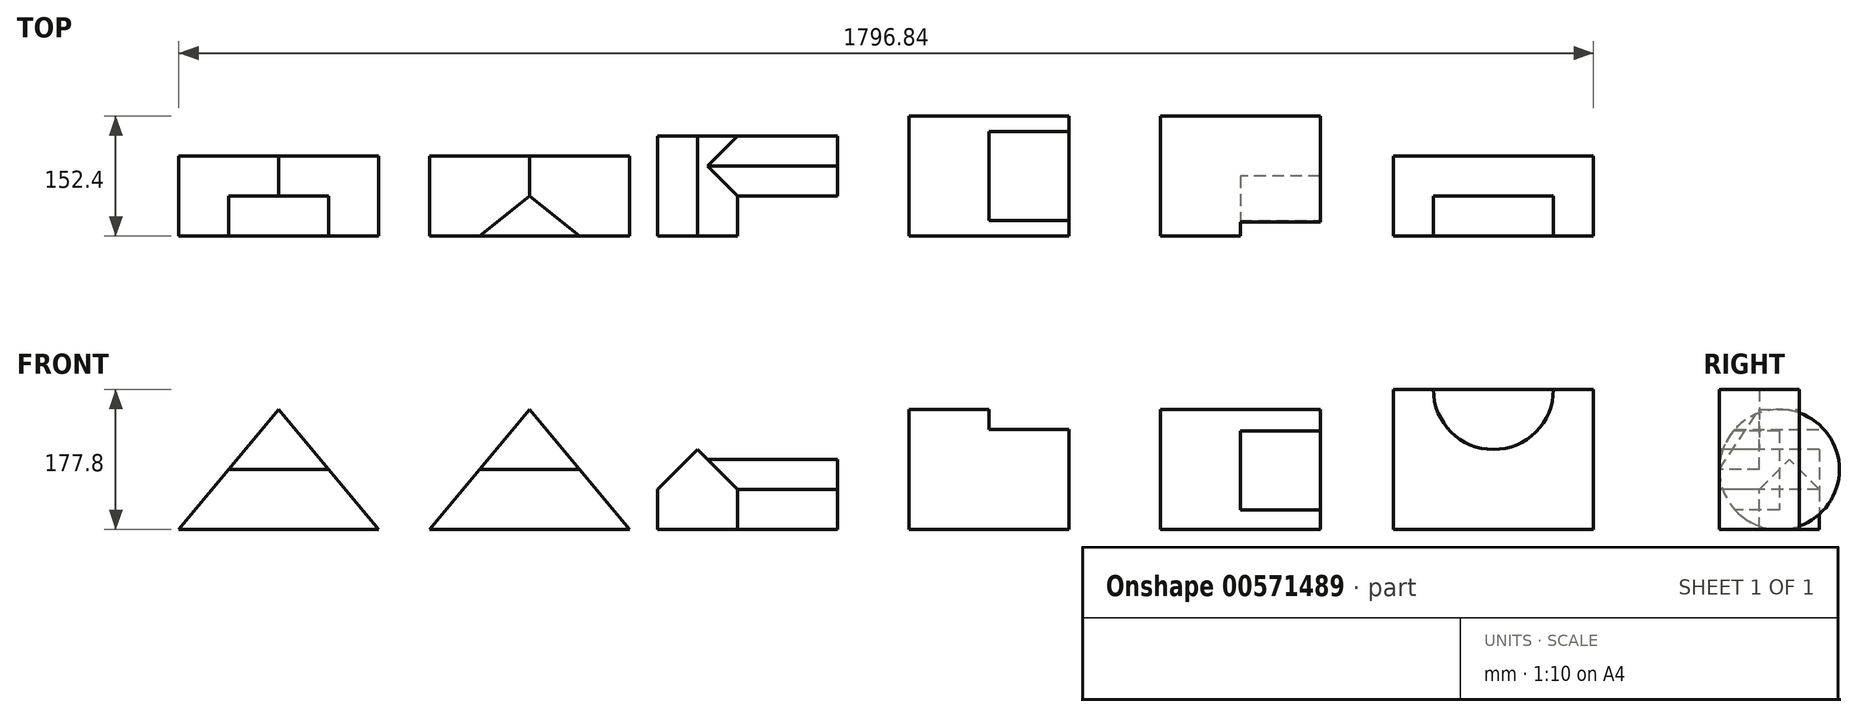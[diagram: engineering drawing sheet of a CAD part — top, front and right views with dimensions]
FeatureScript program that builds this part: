
annotation { "Feature Type Name" : "Feature", "Feature Type Description" : "" }
export const myFeature = defineFeature(function(context is Context, id is Id, definition is map)
    precondition{}
    {
        {
            var Q0;
            Q0=qCreatedBy(makeId("Front.planeOp"),FACE);
            var sketch = newSketch(context, id + "F0", { "sketchPlane" : qUnion([Q0])});
            skLineSegment(sketch, "E0", {"start": v(103.19, 0) * mm, "end": v(103.19, 152.4) * mm});
            skLineSegment(sketch, "E1", {"start": v(103.19, 152.4) * mm, "end": v(357.19, 152.4) * mm});
            skLineSegment(sketch, "E2", {"start": v(357.19, 152.4) * mm, "end": v(357.19, 0) * mm});
            skLineSegment(sketch, "E3", {"start": v(357.19, 0) * mm, "end": v(103.19, 0) * mm});
            skSolve(sketch);
        }
        {
            var Q0;
            Q0=makeQuery(id+"F0.imprint","IMPRINT",FACE,{"disambiguationData":[TD([[makeQuery(id+"F0.imprint","IMPRINT",EDGE,{"derivedFrom":sQuery(id+"F0.wireOp",EDGE,"E0")}),-1.0]])]});
            extrude(context, id + "F1", {"entities" : qUnion([Q0]), "oppositeDirection" : true, "depth" : 101.6 * mm, "offsetDistance" : 25.4 * mm});
        }
        {
            var Q0;
            Q0=makeQuery(id+"F1.opExtrude","CAP_FACE",FACE,{"disambiguationData":[OSD([sQuery(id+"F0.wireOp",EDGE,"E0"),sQuery(id+"F0.wireOp",EDGE,"E1"),sQuery(id+"F0.wireOp",EDGE,"E2"),sQuery(id+"F0.wireOp",EDGE,"E3")])],"isStart":true});
            var sketch = newSketch(context, id + "F2", { "sketchPlane" : qUnion([Q0])});
            skLineSegment(sketch, "E4", {"start": v(103.19, 0) * mm, "end": v(230.19, 152.4) * mm});
            skLineSegment(sketch, "E5", {"start": v(230.19, 152.4) * mm, "end": v(357.19, 0) * mm});
            skLineSegment(sketch, "E6", {"start": v(166.69, 76.2) * mm, "end": v(293.69, 76.2) * mm});
            skSolve(sketch);
        }
        {
            var Q0;
            {var subQ1=makeQuery(id+"F1.opExtrude","CAP_EDGE",EDGE,{"disambiguationData":[OSD([sQuery(id+"F0.wireOp",EDGE,"E0")])],"isStart":true});Q0=makeQuery(id+"F2.imprint","IMPRINT",FACE,{"disambiguationData":[TD([[makeQuery(id+"F2.imprint","IMPRINT",EDGE,{"derivedFrom":subQ1}),-1.0]])]});}
            extrude(context, id + "F3", {"entities" : qUnion([Q0]), "operationType" : NewBodyOperationType.REMOVE, "oppositeDirection" : true, "depth" : 171.45 * mm, "offsetDistance" : 25.4 * mm});
        }
        {
            var Q0;
            Q0=makeQuery(id+"F1.opExtrude","CAP_FACE",FACE,{"disambiguationData":[OSD([sQuery(id+"F0.wireOp",EDGE,"E0"),sQuery(id+"F0.wireOp",EDGE,"E1"),sQuery(id+"F0.wireOp",EDGE,"E2"),sQuery(id+"F0.wireOp",EDGE,"E3")])],"isStart":true});
            var sketch = newSketch(context, id + "F4", { "sketchPlane" : qUnion([Q0])});
            skLineSegment(sketch, "E7", {"start": v(357.19, 0) * mm, "end": v(230.19, 152.4) * mm});
            skLineSegment(sketch, "E8", {"start": v(293.69, 76.2) * mm, "end": v(166.69, 76.2) * mm});
            skSolve(sketch);
        }
        {
            var Q0;
            {var subQ3=sQuery(id+"F4.wireOp",EDGE,"E8");Q0=makeQuery(id+"F4.imprint","IMPRINT",FACE,{"disambiguationData":[TD([[makeQuery(id+"F4.imprint","IMPRINT",EDGE,{"derivedFrom":subQ3}),-1.0]])]});}
            extrude(context, id + "F5", {"entities" : qUnion([Q0]), "operationType" : NewBodyOperationType.REMOVE, "oppositeDirection" : true, "depth" : 50.8 * mm, "offsetDistance" : 25.4 * mm});
        }
        {
            var Q0;
            Q0=makeQuery(id+"F1.opExtrude","CAP_FACE",FACE,{"disambiguationData":[OSD([sQuery(id+"F0.wireOp",EDGE,"E0"),sQuery(id+"F0.wireOp",EDGE,"E1"),sQuery(id+"F0.wireOp",EDGE,"E2"),sQuery(id+"F0.wireOp",EDGE,"E3")])],"isStart":true});
            var sketch = newSketch(context, id + "F6", { "sketchPlane" : qUnion([Q0])});
            skLineSegment(sketch, "E9", {"start": v(293.69, 76.2) * mm, "end": v(357.19, 0) * mm});
            skSolve(sketch);
        }
        {
            var Q0;
            Q0=makeQuery(id+"F6.imprint","IMPRINT",FACE,{"disambiguationData":[TD([[makeQuery(id+"F6.imprint","IMPRINT",EDGE,{"derivedFrom":sQuery(id+"F6.wireOp",EDGE,"E9")}),1.0]])]});
            extrude(context, id + "F7", {"entities" : qUnion([Q0]), "operationType" : NewBodyOperationType.REMOVE, "oppositeDirection" : true, "depth" : 181.1 * mm, "offsetDistance" : 25.4 * mm});
        }
        {
            var Q0;
            Q0=qCreatedBy(makeId("Front.planeOp"),FACE);
            var sketch = newSketch(context, id + "F8", { "sketchPlane" : qUnion([Q0])});
            skLineSegment(sketch, "E10", {"start": v(421.92, 0) * mm, "end": v(421.92, 152.4) * mm});
            skLineSegment(sketch, "E11", {"start": v(421.92, 152.4) * mm, "end": v(675.92, 152.4) * mm});
            skLineSegment(sketch, "E12", {"start": v(675.92, 152.4) * mm, "end": v(675.92, 0) * mm});
            skLineSegment(sketch, "E13", {"start": v(675.92, 0) * mm, "end": v(421.92, 0) * mm});
            skSolve(sketch);
        }
        {
            var Q0;
            Q0=makeQuery(id+"F8.imprint","IMPRINT",FACE,{"disambiguationData":[TD([[makeQuery(id+"F8.imprint","IMPRINT",EDGE,{"derivedFrom":sQuery(id+"F8.wireOp",EDGE,"E10")}),-1.0]])]});
            extrude(context, id + "F9", {"entities" : qUnion([Q0]), "oppositeDirection" : true, "depth" : 101.6 * mm, "offsetDistance" : 25.4 * mm});
        }
        {
            var Q0;
            Q0=makeQuery(id+"F9.opExtrude","SWEPT_FACE",FACE,{"disambiguationData":[OSD([sQuery(id+"F8.wireOp",EDGE,"E12")])]});
            var sketch = newSketch(context, id + "F10", { "sketchPlane" : qUnion([Q0])});
            skLineSegment(sketch, "E14", {"start": v(0, 76.2) * mm, "end": v(50.8, 152.4) * mm});
            skSolve(sketch);
        }
        {
            var Q0;
            {var subQ0=sQuery(id+"F10.wireOp",EDGE,"E14");Q0=makeQuery(id+"F10.imprint","IMPRINT",FACE,{"disambiguationData":[TD([[makeQuery(id+"F10.imprint","IMPRINT",EDGE,{"derivedFrom":subQ0}),1.0]])]});}
            extrude(context, id + "F11", {"entities" : qUnion([Q0]), "operationType" : NewBodyOperationType.REMOVE, "oppositeDirection" : true, "depth" : 317.75 * mm, "offsetDistance" : 25.4 * mm});
        }
        {
            var Q0;
            Q0=makeQuery(id+"F9.opExtrude","CAP_FACE",FACE,{"disambiguationData":[OSD([sQuery(id+"F8.wireOp",EDGE,"E10"),sQuery(id+"F8.wireOp",EDGE,"E11"),sQuery(id+"F8.wireOp",EDGE,"E12"),sQuery(id+"F8.wireOp",EDGE,"E13")])],"isStart":false});
            var sketch = newSketch(context, id + "F12", { "sketchPlane" : qUnion([Q0])});
            skLineSegment(sketch, "E15", {"start": v(-675.92, 0) * mm, "end": v(-548.92, 152.4) * mm});
            skSolve(sketch);
        }
        {
            var Q0;
            {var subQ0=sQuery(id+"F12.wireOp",EDGE,"E15");Q0=makeQuery(id+"F12.imprint","IMPRINT",FACE,{"disambiguationData":[TD([[makeQuery(id+"F12.imprint","IMPRINT",EDGE,{"derivedFrom":subQ0}),1.0]])]});}
            extrude(context, id + "F13", {"entities" : qUnion([Q0]), "operationType" : NewBodyOperationType.REMOVE, "oppositeDirection" : true, "depth" : 144.78 * mm, "offsetDistance" : 25.4 * mm});
        }
        {
            var Q0;
            Q0=makeQuery(id+"F9.opExtrude","CAP_FACE",FACE,{"disambiguationData":[OSD([sQuery(id+"F8.wireOp",EDGE,"E10"),sQuery(id+"F8.wireOp",EDGE,"E11"),sQuery(id+"F8.wireOp",EDGE,"E12"),sQuery(id+"F8.wireOp",EDGE,"E13")])],"isStart":false});
            var sketch = newSketch(context, id + "F14", { "sketchPlane" : qUnion([Q0])});
            skLineSegment(sketch, "E16", {"start": v(-548.92, 152.4) * mm, "end": v(-421.92, 0) * mm});
            skSolve(sketch);
        }
        {
            var Q0;
            Q0=makeQuery(id+"F14.imprint","IMPRINT",FACE,{"disambiguationData":[TD([[makeQuery(id+"F14.imprint","IMPRINT",EDGE,{"derivedFrom":sQuery(id+"F14.wireOp",EDGE,"E16")}),1.0]])]});
            extrude(context, id + "F15", {"entities" : qUnion([Q0]), "operationType" : NewBodyOperationType.REMOVE, "oppositeDirection" : true, "depth" : 111.76 * mm, "offsetDistance" : 25.4 * mm});
        }
        {
            var Q0;
            Q0=qCreatedBy(makeId("Top.planeOp"),FACE);
            var sketch = newSketch(context, id + "F16", { "sketchPlane" : qUnion([Q0])});
            skLineSegment(sketch, "E17", {"start": v(711.33, 0) * mm, "end": v(711.33, 127) * mm});
            skLineSegment(sketch, "E18", {"start": v(711.33, 127) * mm, "end": v(939.93, 127) * mm});
            skLineSegment(sketch, "E19", {"start": v(939.93, 127) * mm, "end": v(939.93, 0) * mm});
            skLineSegment(sketch, "E20", {"start": v(939.93, 0) * mm, "end": v(711.33, 0) * mm});
            skSolve(sketch);
        }
        {
            var Q0;
            Q0=makeQuery(id+"F16.imprint","IMPRINT",FACE,{"disambiguationData":[TD([[makeQuery(id+"F16.imprint","IMPRINT",EDGE,{"derivedFrom":sQuery(id+"F16.wireOp",EDGE,"E17")}),-1.0]])]});
            extrude(context, id + "F17", {"entities" : qUnion([Q0]), "depth" : 101.6 * mm, "offsetDistance" : 25.4 * mm});
        }
        {
            var Q0;
            Q0=makeQuery(id+"F17.opExtrude","CAP_FACE",FACE,{"disambiguationData":[OSD([sQuery(id+"F16.wireOp",EDGE,"E17"),sQuery(id+"F16.wireOp",EDGE,"E18"),sQuery(id+"F16.wireOp",EDGE,"E19"),sQuery(id+"F16.wireOp",EDGE,"E20")])],"isStart":false});
            var sketch = newSketch(context, id + "F18", { "sketchPlane" : qUnion([Q0])});
            skLineSegment(sketch, "E21.bottom", {"start": v(939.93, 0) * mm, "end": v(812.93, 0) * mm});
            skLineSegment(sketch, "E21.top", {"start": v(939.93, 50.8) * mm, "end": v(812.93, 50.8) * mm});
            skLineSegment(sketch, "E21.left", {"start": v(939.93, 0) * mm, "end": v(939.93, 50.8) * mm});
            skLineSegment(sketch, "E21.right", {"start": v(812.93, 0) * mm, "end": v(812.93, 50.8) * mm});
            skSolve(sketch);
        }
        {
            var Q0;
            Q0=makeQuery(id+"F18.imprint","IMPRINT",FACE,{"disambiguationData":[TD([[makeQuery(id+"F18.imprint","IMPRINT",EDGE,{"derivedFrom":sQuery(id+"F18.wireOp",EDGE,"E21.bottom")}),-1.0]])]});
            extrude(context, id + "F19", {"entities" : qUnion([Q0]), "operationType" : NewBodyOperationType.REMOVE, "oppositeDirection" : true, "depth" : 124.46 * mm, "offsetDistance" : 25.4 * mm});
        }
        {
            var Q0;
            Q0=makeQuery(id+"F17.opExtrude","SWEPT_FACE",FACE,{"disambiguationData":[OSD([sQuery(id+"F16.wireOp",EDGE,"E19")])]});
            var sketch = newSketch(context, id + "F20", { "sketchPlane" : qUnion([Q0])});
            skLineSegment(sketch, "E22.bottom", {"start": v(50.8, 101.6) * mm, "end": v(127, 101.6) * mm});
            skLineSegment(sketch, "E22.top", {"start": v(50.8, 88.9) * mm, "end": v(127, 88.9) * mm});
            skLineSegment(sketch, "E22.left", {"start": v(50.8, 101.6) * mm, "end": v(50.8, 88.9) * mm});
            skLineSegment(sketch, "E22.right", {"start": v(127, 101.6) * mm, "end": v(127, 88.9) * mm});
            skSolve(sketch);
        }
        {
            var Q0;
            Q0=makeQuery(id+"F20.imprint","IMPRINT",FACE,{"disambiguationData":[TD([[makeQuery(id+"F20.imprint","IMPRINT",EDGE,{"derivedFrom":sQuery(id+"F20.wireOp",EDGE,"E22.bottom")}),1.0]])]});
            extrude(context, id + "F21", {"entities" : qUnion([Q0]), "operationType" : NewBodyOperationType.REMOVE, "oppositeDirection" : true, "depth" : 127 * mm, "offsetDistance" : 25.4 * mm});
        }
        {
            var Q0;
            Q0=makeQuery(id+"F17.opExtrude","SWEPT_FACE",FACE,{"disambiguationData":[OSD([sQuery(id+"F16.wireOp",EDGE,"E20")])]});
            var sketch = newSketch(context, id + "F22", { "sketchPlane" : qUnion([Q0])});
            skLineSegment(sketch, "E23", {"start": v(762.13, 101.6) * mm, "end": v(711.33, 50.8) * mm});
            skSolve(sketch);
        }
        {
            var Q0;
            {var subQ0=sQuery(id+"F22.wireOp",EDGE,"E23");Q0=makeQuery(id+"F22.imprint","IMPRINT",FACE,{"disambiguationData":[TD([[makeQuery(id+"F22.imprint","IMPRINT",EDGE,{"derivedFrom":subQ0}),-1.0]])]});}
            extrude(context, id + "F23", {"entities" : qUnion([Q0]), "operationType" : NewBodyOperationType.REMOVE, "oppositeDirection" : true, "depth" : 210.82 * mm, "offsetDistance" : 25.4 * mm});
        }
        {
            var Q0;
            Q0=makeQuery(id+"F17.opExtrude","SWEPT_FACE",FACE,{"disambiguationData":[OSD([sQuery(id+"F16.wireOp",EDGE,"E19")])]});
            var sketch = newSketch(context, id + "F24", { "sketchPlane" : qUnion([Q0])});
            skLineSegment(sketch, "E24", {"start": v(127, 0) * mm, "end": v(127, 50.8) * mm});
            skLineSegment(sketch, "E25", {"start": v(127, 50.8) * mm, "end": v(88.9, 88.9) * mm});
            skSolve(sketch);
        }
        {
            var Q0;
            {var subQ0=sQuery(id+"F24.wireOp",EDGE,"E25");Q0=makeQuery(id+"F24.imprint","IMPRINT",FACE,{"disambiguationData":[TD([[makeQuery(id+"F24.imprint","IMPRINT",EDGE,{"derivedFrom":subQ0}),-1.0]])]});}
            extrude(context, id + "F25", {"entities" : qUnion([Q0]), "operationType" : NewBodyOperationType.REMOVE, "oppositeDirection" : true, "depth" : 127 * mm, "offsetDistance" : 25.4 * mm});
        }
        {
            var Q0;
            Q0=makeQuery(id+"F17.opExtrude","SWEPT_FACE",FACE,{"disambiguationData":[OSD([sQuery(id+"F16.wireOp",EDGE,"E19")])]});
            var sketch = newSketch(context, id + "F26", { "sketchPlane" : qUnion([Q0])});
            skLineSegment(sketch, "E26", {"start": v(50.8, 0) * mm, "end": v(50.8, 50.8) * mm});
            skLineSegment(sketch, "E27", {"start": v(50.8, 50.8) * mm, "end": v(88.9, 88.9) * mm});
            skSolve(sketch);
        }
        {
            var Q0;
            {var subQ0=sQuery(id+"F26.wireOp",EDGE,"E27");Q0=makeQuery(id+"F26.imprint","IMPRINT",FACE,{"disambiguationData":[TD([[makeQuery(id+"F26.imprint","IMPRINT",EDGE,{"derivedFrom":subQ0}),1.0]])]});}
            extrude(context, id + "F27", {"entities" : qUnion([Q0]), "operationType" : NewBodyOperationType.REMOVE, "oppositeDirection" : true, "depth" : 127 * mm, "offsetDistance" : 25.4 * mm});
        }
        {
            var Q0;
            Q0=makeQuery(id+"F17.opExtrude","SWEPT_FACE",FACE,{"disambiguationData":[OSD([sQuery(id+"F16.wireOp",EDGE,"E20")])]});
            var sketch = newSketch(context, id + "F28", { "sketchPlane" : qUnion([Q0])});
            skLineSegment(sketch, "E28", {"start": v(812.93, 50.8) * mm, "end": v(762.13, 101.6) * mm});
            skSolve(sketch);
        }
        {
            var Q0;
            {var subQ0=sQuery(id+"F28.wireOp",EDGE,"E28");Q0=makeQuery(id+"F28.imprint","IMPRINT",FACE,{"disambiguationData":[TD([[makeQuery(id+"F28.imprint","IMPRINT",EDGE,{"derivedFrom":subQ0}),-1.0]])]});}
            extrude(context, id + "F29", {"entities" : qUnion([Q0]), "operationType" : NewBodyOperationType.REMOVE, "oppositeDirection" : true, "depth" : 157.48 * mm, "offsetDistance" : 25.4 * mm});
        }
        {
            var Q0;
            Q0=makeQuery(id+"F17.opExtrude","SWEPT_FACE",FACE,{"disambiguationData":[OSD([sQuery(id+"F16.wireOp",EDGE,"E19")])]});
            var sketch = newSketch(context, id + "F30", { "sketchPlane" : qUnion([Q0])});
            skLineSegment(sketch, "E29", {"start": v(50.8, 50.8) * mm, "end": v(127, 50.8) * mm});
            skSolve(sketch);
        }
        {
            var Q0;
            Q0=makeQuery(id+"F30.imprint","IMPRINT",FACE,{"disambiguationData":[TD([[makeQuery(id+"F30.imprint","IMPRINT",EDGE,{"derivedFrom":sQuery(id+"F30.wireOp",EDGE,"E29")}),1.0]])]});
            extrude(context, id + "F31", {"entities" : qUnion([Q0]), "operationType" : NewBodyOperationType.ADD, "oppositeDirection" : true, "depth" : 177.8 * mm, "offsetDistance" : 25.4 * mm});
        }
        {
            var Q0;
            Q0=qCreatedBy(makeId("Top.planeOp"),FACE);
            var sketch = newSketch(context, id + "F32", { "sketchPlane" : qUnion([Q0])});
            skLineSegment(sketch, "E30", {"start": v(1030.46, 0) * mm, "end": v(1030.46, 152.4) * mm});
            skLineSegment(sketch, "E31", {"start": v(1030.46, 152.4) * mm, "end": v(1233.66, 152.4) * mm});
            skLineSegment(sketch, "E32", {"start": v(1233.66, 152.4) * mm, "end": v(1233.66, 0) * mm});
            skLineSegment(sketch, "E33", {"start": v(1233.66, 0) * mm, "end": v(1030.46, 0) * mm});
            skSolve(sketch);
        }
        {
            var Q0;
            Q0=makeQuery(id+"F32.imprint","IMPRINT",FACE,{"disambiguationData":[TD([[makeQuery(id+"F32.imprint","IMPRINT",EDGE,{"derivedFrom":sQuery(id+"F32.wireOp",EDGE,"E30")}),-1.0]])]});
            extrude(context, id + "F33", {"entities" : qUnion([Q0]), "depth" : 152.4 * mm, "offsetDistance" : 25.4 * mm});
        }
        {
            var Q0;
            Q0=makeQuery(id+"F33.opExtrude","SWEPT_FACE",FACE,{"disambiguationData":[OSD([sQuery(id+"F32.wireOp",EDGE,"E32")])]});
            var sketch = newSketch(context, id + "F34", { "sketchPlane" : qUnion([Q0])});
            skLineSegment(sketch, "E34.bottom", {"start": v(0, 152.4) * mm, "end": v(152.4, 152.4) * mm});
            skLineSegment(sketch, "E34.top", {"start": v(0, 127) * mm, "end": v(152.4, 127) * mm});
            skLineSegment(sketch, "E34.left", {"start": v(0, 152.4) * mm, "end": v(0, 127) * mm});
            skLineSegment(sketch, "E34.right", {"start": v(152.4, 152.4) * mm, "end": v(152.4, 127) * mm});
            skSolve(sketch);
        }
        {
            var Q0;
            Q0=makeQuery(id+"F34.imprint","IMPRINT",FACE,{"disambiguationData":[TD([[makeQuery(id+"F34.imprint","IMPRINT",EDGE,{"derivedFrom":sQuery(id+"F34.wireOp",EDGE,"E34.bottom")}),1.0]])]});
            extrude(context, id + "F35", {"entities" : qUnion([Q0]), "operationType" : NewBodyOperationType.REMOVE, "oppositeDirection" : true, "depth" : 101.6 * mm, "offsetDistance" : 25.4 * mm});
        }
        {
            var Q0;
            Q0=makeQuery(id+"F33.opExtrude","CAP_EDGE",EDGE,{"disambiguationData":[OSD([sQuery(id+"F32.wireOp",EDGE,"E31")])],"isStart":false});
            fillet(context, id + "F36", {"entities" : qUnion([Q0]), "radius" : 76.2 * mm, "tangentPropagation" : true, "allowEdgeOverflow" : false});
        }
        {
            var Q0;
            Q0=makeQuery(id+"F33.opExtrude","CAP_EDGE",EDGE,{"disambiguationData":[OSD([sQuery(id+"F32.wireOp",EDGE,"E33")])],"isStart":false});
            fillet(context, id + "F37", {"entities" : qUnion([Q0]), "radius" : 76.2 * mm, "tangentPropagation" : true, "allowEdgeOverflow" : false});
        }
        {
            var Q0;
            Q0=makeQuery(id+"F33.opExtrude","CAP_EDGE",EDGE,{"disambiguationData":[OSD([sQuery(id+"F32.wireOp",EDGE,"E31")])],"isStart":true});
            fillet(context, id + "F38", {"entities" : qUnion([Q0]), "radius" : 76.2 * mm, "tangentPropagation" : true, "allowEdgeOverflow" : false});
        }
        {
            var Q0;
            Q0=makeQuery(id+"F33.opExtrude","CAP_EDGE",EDGE,{"disambiguationData":[OSD([sQuery(id+"F32.wireOp",EDGE,"E33")])],"isStart":true});
            fillet(context, id + "F39", {"entities" : qUnion([Q0]), "radius" : 76.2 * mm, "tangentPropagation" : true, "allowEdgeOverflow" : false});
        }
        {
            var Q0;
            Q0=qCreatedBy(makeId("Top.planeOp"),FACE);
            var sketch = newSketch(context, id + "F40", { "sketchPlane" : qUnion([Q0])});
            skLineSegment(sketch, "E35", {"start": v(1349.86, 0) * mm, "end": v(1349.86, 152.4) * mm});
            skLineSegment(sketch, "E36", {"start": v(1349.86, 152.4) * mm, "end": v(1553.06, 152.4) * mm});
            skLineSegment(sketch, "E37", {"start": v(1553.06, 152.4) * mm, "end": v(1553.06, 0) * mm});
            skLineSegment(sketch, "E38", {"start": v(1553.06, 0) * mm, "end": v(1349.86, 0) * mm});
            skSolve(sketch);
        }
        {
            var Q0;
            Q0=makeQuery(id+"F40.imprint","IMPRINT",FACE,{"disambiguationData":[TD([[makeQuery(id+"F40.imprint","IMPRINT",EDGE,{"derivedFrom":sQuery(id+"F40.wireOp",EDGE,"E35")}),-1.0]])]});
            extrude(context, id + "F41", {"entities" : qUnion([Q0]), "depth" : 152.4 * mm, "offsetDistance" : 25.4 * mm});
        }
        {
            var Q0;
            Q0=makeQuery(id+"F41.opExtrude","SWEPT_FACE",FACE,{"disambiguationData":[OSD([sQuery(id+"F40.wireOp",EDGE,"E38")])]});
            var sketch = newSketch(context, id + "F42", { "sketchPlane" : qUnion([Q0])});
            skLineSegment(sketch, "E39", {"start": v(1553.06, 124.92) * mm, "end": v(1451.52, 124.92) * mm});
            skLineSegment(sketch, "E40", {"start": v(1451.52, 124.92) * mm, "end": v(1451.52, 25.04) * mm});
            skLineSegment(sketch, "E41", {"start": v(1451.52, 25.04) * mm, "end": v(1553.06, 25.04) * mm});
            skSolve(sketch);
        }
        {
            var Q0;
            {var subQ0=sQuery(id+"F42.wireOp",EDGE,"E39");Q0=makeQuery(id+"F42.imprint","IMPRINT",FACE,{"disambiguationData":[TD([[makeQuery(id+"F42.imprint","IMPRINT",EDGE,{"derivedFrom":subQ0}),1.0]])]});}
            extrude(context, id + "F43", {"entities" : qUnion([Q0]), "operationType" : NewBodyOperationType.REMOVE, "oppositeDirection" : true, "depth" : 76.2 * mm, "offsetDistance" : 25.4 * mm});
        }
        {
            var Q0;
            Q0=makeQuery(id+"F41.opExtrude","CAP_EDGE",EDGE,{"disambiguationData":[OSD([sQuery(id+"F40.wireOp",EDGE,"E38")])],"isStart":false});
            fillet(context, id + "F44", {"entities" : qUnion([Q0]), "radius" : 76.2 * mm, "tangentPropagation" : true, "allowEdgeOverflow" : false});
        }
        {
            var Q0;
            Q0=makeQuery(id+"F41.opExtrude","CAP_EDGE",EDGE,{"disambiguationData":[OSD([sQuery(id+"F40.wireOp",EDGE,"E38")])],"isStart":true});
            var Q1;
            Q1=makeQuery(id+"F41.opExtrude","CAP_EDGE",EDGE,{"disambiguationData":[OSD([sQuery(id+"F40.wireOp",EDGE,"E36")])],"isStart":false});
            var Q2;
            Q2=makeQuery(id+"F41.opExtrude","CAP_EDGE",EDGE,{"disambiguationData":[OSD([sQuery(id+"F40.wireOp",EDGE,"E36")])],"isStart":true});
            fillet(context, id + "F45", {"entities" : qUnion([Q0, Q1, Q2]), "radius" : 76.2 * mm, "tangentPropagation" : true, "allowEdgeOverflow" : false});
        }
        {
            var Q0;
            Q0=qCreatedBy(makeId("Top.planeOp"),FACE);
            var sketch = newSketch(context, id + "F46", { "sketchPlane" : qUnion([Q0])});
            skLineSegment(sketch, "E42", {"start": v(1646.03, 0) * mm, "end": v(1646.03, 101.6) * mm});
            skLineSegment(sketch, "E43", {"start": v(1646.03, 101.6) * mm, "end": v(1900.03, 101.6) * mm});
            skLineSegment(sketch, "E44", {"start": v(1900.03, 101.6) * mm, "end": v(1900.03, 0) * mm});
            skLineSegment(sketch, "E45", {"start": v(1900.03, 0) * mm, "end": v(1646.03, 0) * mm});
            skSolve(sketch);
        }
        {
            var Q0;
            Q0=makeQuery(id+"F46.imprint","IMPRINT",FACE,{"disambiguationData":[TD([[makeQuery(id+"F46.imprint","IMPRINT",EDGE,{"derivedFrom":sQuery(id+"F46.wireOp",EDGE,"E42")}),-1.0]])]});
            extrude(context, id + "F47", {"entities" : qUnion([Q0]), "depth" : 177.8 * mm, "offsetDistance" : 25.4 * mm});
        }
        {
            var Q0;
            Q0=makeQuery(id+"F47.opExtrude","SWEPT_FACE",FACE,{"disambiguationData":[OSD([sQuery(id+"F46.wireOp",EDGE,"E45")])]});
            var sketch = newSketch(context, id + "F48", { "sketchPlane" : qUnion([Q0])});
            skCircle(sketch, "E46", {"center": v(1773.03, 177.8) * mm, "radius": 76.2 * mm});
            skSolve(sketch);
        }
        {
            var Q0;
            {var subQ0=sQuery(id+"F48.wireOp",EDGE,"E46");var subQ1=makeQuery(id+"F47.opExtrude","CAP_EDGE",EDGE,{"disambiguationData":[OSD([sQuery(id+"F46.wireOp",EDGE,"E45")])],"isStart":false});var subQ2=makeQuery(id+"F48.imprint","INTERSECT",VERTEX,{"disambiguationData":[OD(0.0)],"derivedFrom":[subQ1,subQ0]});Q0=makeQuery(id+"F48.imprint","IMPRINT",FACE,{"disambiguationData":[TD([[makeQuery(id+"F48.imprint","IMPRINT",EDGE,{"disambiguationData":[TD([[subQ2,-1.0]])],"derivedFrom":subQ0}),1.0]])]});}
            extrude(context, id + "F49", {"entities" : qUnion([Q0]), "operationType" : NewBodyOperationType.REMOVE, "oppositeDirection" : true, "depth" : 50.8 * mm, "offsetDistance" : 25.4 * mm});
        }
    });
